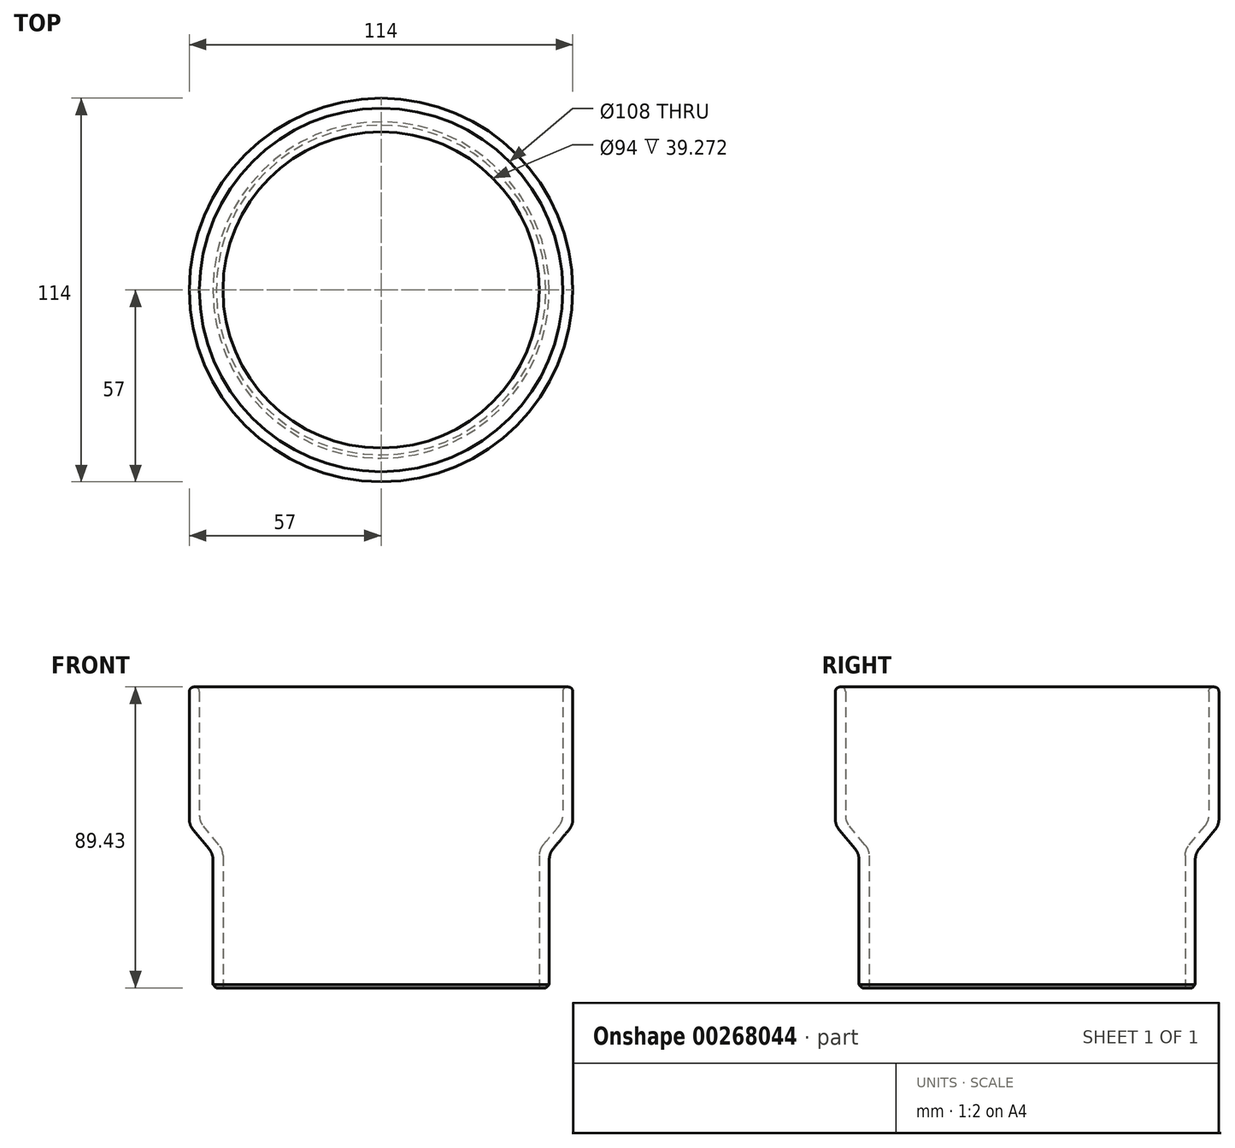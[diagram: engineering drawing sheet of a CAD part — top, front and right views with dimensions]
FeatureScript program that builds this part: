
annotation { "Feature Type Name" : "Feature", "Feature Type Description" : "" }
export const myFeature = defineFeature(function(context is Context, id is Id, definition is map)
    precondition{}
    {
        {
            var Q0;
            Q0=qCreatedBy(makeId("Front.planeOp"),FACE);
            var sketch = newSketch(context, id + "F0", { "sketchPlane" : qUnion([Q0])});
            skLineSegment(sketch, "E0.top", {"start": v(47, 0) * mm, "end": v(50, 0) * mm});
            skLineSegment(sketch, "E0.right", {"start": v(50, 40) * mm, "end": v(50, 0) * mm});
            skLineSegment(sketch, "E1", {"start": v(0, -11.04) * mm, "end": v(0, 23.12) * mm, "construction": true});
            skLineSegment(sketch, "E2", {"start": v(0, 23.12) * mm, "end": v(0, 77.14) * mm, "construction": true});
            skLineSegment(sketch, "E3.top", {"start": v(57, 89.43) * mm, "end": v(54, 89.43) * mm});
            skLineSegment(sketch, "E3.right", {"start": v(54, 49.43) * mm, "end": v(54, 89.43) * mm});
            skLineSegment(sketch, "E4", {"start": v(57, 89.43) * mm, "end": v(57, 48.34) * mm});
            skLineSegment(sketch, "E5", {"start": v(50, 40) * mm, "end": v(57, 48.34) * mm});
            skLineSegment(sketch, "E6.0", {"start": v(47.87, 42.13) * mm, "end": v(54, 49.43) * mm});
            skLineSegment(sketch, "E7", {"start": v(52.63, 47.8) * mm, "end": v(47, 41.1) * mm});
            skLineSegment(sketch, "E8", {"start": v(47, 0) * mm, "end": v(47, 41.1) * mm});
            skSolve(sketch);
        }
        {
            var Q0;
            Q0=makeQuery(id+"F0.imprint","IMPRINT",FACE,{"disambiguationData":[TD([[makeQuery(id+"F0.imprint","IMPRINT",EDGE,{"derivedFrom":sQuery(id+"F0.wireOp",EDGE,"E0.top")}),1.0]])]});
            var Q1;
            Q1=sQuery(id+"F0.wireOp",EDGE,"E1");
            revolve(context, id + "F1", {"entities" : qUnion([Q0]), "axis" : qUnion([Q1]), "revolveType" : RevolveType.FULL});
        }
        {
            var Q0;
            Q0=makeQuery(id+"F1.opRevolve","SWEPT_EDGE",EDGE,{"disambiguationData":[OSD([sQuery(id+"F0.wireOp",EDGE,"E4"),sQuery(id+"F0.wireOp",EDGE,"E5")])]});
            var Q1;
            Q1=makeQuery(id+"F1.opRevolve","SWEPT_EDGE",EDGE,{"disambiguationData":[OSD([sQuery(id+"F0.wireOp",EDGE,"E0.right"),sQuery(id+"F0.wireOp",EDGE,"E5")])]});
            var Q2;
            Q2=makeQuery(id+"F1.opRevolve","SWEPT_EDGE",EDGE,{"disambiguationData":[OSD([sQuery(id+"F0.wireOp",EDGE,"E3.right"),sQuery(id+"F0.wireOp",EDGE,"E6.0")])]});
            var Q3;
            Q3=makeQuery(id+"F1.opRevolve","SWEPT_EDGE",EDGE,{"disambiguationData":[OSD([sQuery(id+"F0.wireOp",EDGE,"E7"),sQuery(id+"F0.wireOp",EDGE,"E8")])]});
            fillet(context, id + "F2", {"entities" : qUnion([Q0, Q1, Q2, Q3]), "radius" : 5 * mm, "tangentPropagation" : true, "allowEdgeOverflow" : false});
        }
        {
            var Q0;
            Q0=makeQuery(id+"F1.opRevolve","SWEPT_EDGE",EDGE,{"disambiguationData":[OSD([sQuery(id+"F0.wireOp",EDGE,"E3.top"),sQuery(id+"F0.wireOp",EDGE,"E4")])]});
            var Q1;
            Q1=makeQuery(id+"F1.opRevolve","SWEPT_EDGE",EDGE,{"disambiguationData":[OSD([sQuery(id+"F0.wireOp",EDGE,"E3.top"),sQuery(id+"F0.wireOp",EDGE,"E3.right")])]});
            fillet(context, id + "F3", {"entities" : qUnion([Q0, Q1]), "radius" : 1.4 * mm, "tangentPropagation" : true, "allowEdgeOverflow" : false});
        }
        {
            var Q0;
            Q0=makeQuery(id+"F1.opRevolve","SWEPT_EDGE",EDGE,{"disambiguationData":[OSD([sQuery(id+"F0.wireOp",EDGE,"E0.top"),sQuery(id+"F0.wireOp",EDGE,"E0.right")])]});
            chamfer(context, id + "F4", {"entities" : qUnion([Q0]), "width" : 1 * mm, "tangentPropagation" : true});
        }
    });
